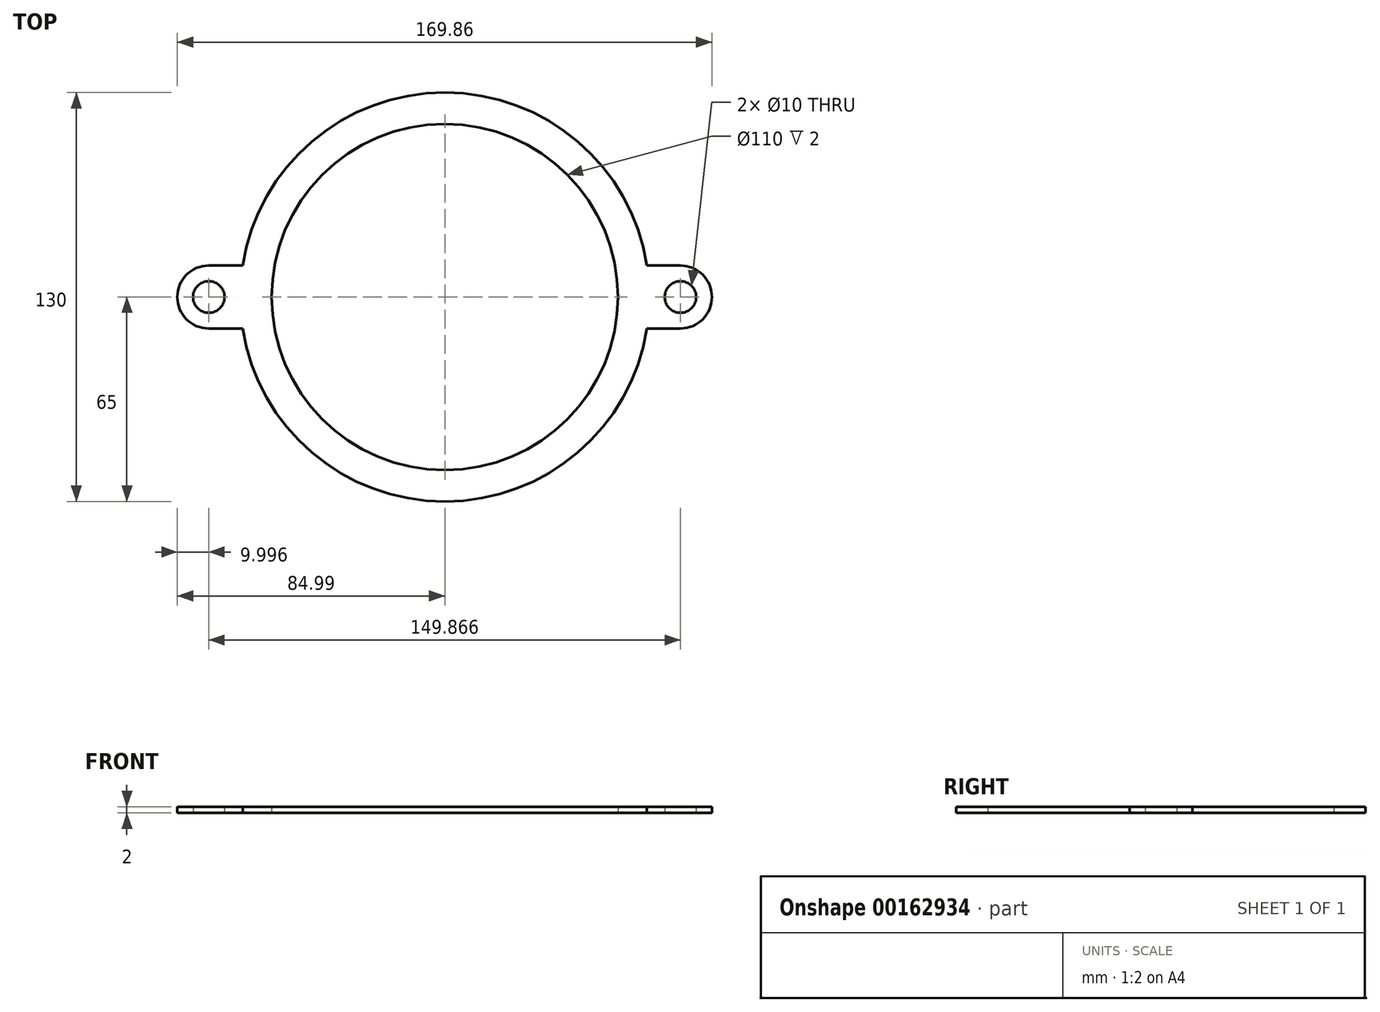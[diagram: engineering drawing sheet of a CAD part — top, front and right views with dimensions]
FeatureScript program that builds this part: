
annotation { "Feature Type Name" : "Feature", "Feature Type Description" : "" }
export const myFeature = defineFeature(function(context is Context, id is Id, definition is map)
    precondition{}
    {
        {
            var Q0;
            Q0=qCreatedBy(makeId("Top.planeOp"),FACE);
            var sketch = newSketch(context, id + "F0", { "sketchPlane" : qUnion([Q0])});
            skCircle(sketch, "E0", {"center": v(0, 0) * mm, "radius": 65 * mm});
            skCircle(sketch, "E1", {"center": v(0, 0) * mm, "radius": 55 * mm});
            skLineSegment(sketch, "E2.bottom", {"start": v(85, 10) * mm, "end": v(-85, 10) * mm});
            skLineSegment(sketch, "E2.top", {"start": v(85, -10) * mm, "end": v(-85, -10) * mm});
            skLineSegment(sketch, "E2.left", {"start": v(85, 10) * mm, "end": v(85, -10) * mm});
            skLineSegment(sketch, "E2.right", {"start": v(-85, 10) * mm, "end": v(-85, -10) * mm});
            skCircle(sketch, "E3", {"center": v(-75, 0) * mm, "radius": 10 * mm});
            skCircle(sketch, "E4", {"center": v(-75, 0) * mm, "radius": 5 * mm});
            skCircle(sketch, "E5", {"center": v(74.87, 0) * mm, "radius": 10 * mm});
            skCircle(sketch, "E6", {"center": v(74.87, 0) * mm, "radius": 5 * mm});
            skSolve(sketch);
        }
        {
            var Q0;
            {var subQ0=sQuery(id+"F0.wireOp",EDGE,"E2.bottom");var subQ1=sQuery(id+"F0.wireOp",EDGE,"E0");var subQ2=makeQuery(id+"F0.imprint","INTERSECT",VERTEX,{"disambiguationData":[OD(0.0)],"derivedFrom":[subQ1,subQ0]});Q0=makeQuery(id+"F0.imprint","IMPRINT",FACE,{"disambiguationData":[TD([[makeQuery(id+"F0.imprint","IMPRINT",EDGE,{"disambiguationData":[TD([[subQ2,-1.0]])],"derivedFrom":subQ1}),1.0]])]});}
            var Q1;
            {var subQ0=sQuery(id+"F0.wireOp",EDGE,"E2.bottom");var subQ1=sQuery(id+"F0.wireOp",EDGE,"E0");var subQ2=makeQuery(id+"F0.imprint","INTERSECT",VERTEX,{"disambiguationData":[OD(0.0)],"derivedFrom":[subQ1,subQ0]});Q1=makeQuery(id+"F0.imprint","IMPRINT",FACE,{"disambiguationData":[TD([[makeQuery(id+"F0.imprint","IMPRINT",EDGE,{"disambiguationData":[TD([[subQ2,1.0]])],"derivedFrom":subQ1}),1.0]])]});}
            var Q2;
            {var subQ0=sQuery(id+"F0.wireOp",EDGE,"E2.bottom");var subQ1=sQuery(id+"F0.wireOp",EDGE,"E0");var subQ2=makeQuery(id+"F0.imprint","INTERSECT",VERTEX,{"disambiguationData":[OD(0.0)],"derivedFrom":[subQ1,subQ0]});Q2=makeQuery(id+"F0.imprint","IMPRINT",FACE,{"disambiguationData":[TD([[makeQuery(id+"F0.imprint","IMPRINT",EDGE,{"disambiguationData":[TD([[subQ2,1.0]])],"derivedFrom":subQ1}),-1.0]])]});}
            var Q3;
            Q3=makeQuery(id+"F0.imprint","IMPRINT",FACE,{"disambiguationData":[TD([[makeQuery(id+"F0.imprint","IMPRINT",EDGE,{"derivedFrom":sQuery(id+"F0.wireOp",EDGE,"E6")}),-1.0]])]});
            var Q4;
            {var subQ0=sQuery(id+"F0.wireOp",EDGE,"E2.top");var subQ1=sQuery(id+"F0.wireOp",EDGE,"E0");var subQ2=makeQuery(id+"F0.imprint","INTERSECT",VERTEX,{"disambiguationData":[OD(1.0)],"derivedFrom":[subQ1,subQ0]});Q4=makeQuery(id+"F0.imprint","IMPRINT",FACE,{"disambiguationData":[TD([[makeQuery(id+"F0.imprint","IMPRINT",EDGE,{"disambiguationData":[TD([[subQ2,-1.0]])],"derivedFrom":subQ1}),-1.0]])]});}
            var Q5;
            {var subQ0=sQuery(id+"F0.wireOp",EDGE,"E2.top");var subQ1=sQuery(id+"F0.wireOp",EDGE,"E0");var subQ2=makeQuery(id+"F0.imprint","INTERSECT",VERTEX,{"disambiguationData":[OD(0.0)],"derivedFrom":[subQ1,subQ0]});Q5=makeQuery(id+"F0.imprint","IMPRINT",FACE,{"disambiguationData":[TD([[makeQuery(id+"F0.imprint","IMPRINT",EDGE,{"disambiguationData":[TD([[subQ2,-1.0]])],"derivedFrom":subQ1}),1.0]])]});}
            var Q6;
            Q6=makeQuery(id+"F0.imprint","IMPRINT",FACE,{"disambiguationData":[TD([[makeQuery(id+"F0.imprint","IMPRINT",EDGE,{"derivedFrom":sQuery(id+"F0.wireOp",EDGE,"E4")}),-1.0]])]});
            var Q7;
            {var subQ0=sQuery(id+"F0.wireOp",EDGE,"E2.top");var subQ1=sQuery(id+"F0.wireOp",EDGE,"E0");var subQ2=makeQuery(id+"F0.imprint","INTERSECT",VERTEX,{"disambiguationData":[OD(0.0)],"derivedFrom":[subQ1,subQ0]});Q7=makeQuery(id+"F0.imprint","IMPRINT",FACE,{"disambiguationData":[TD([[makeQuery(id+"F0.imprint","IMPRINT",EDGE,{"disambiguationData":[TD([[subQ2,1.0]])],"derivedFrom":subQ1}),-1.0]])]});}
            var Q8;
            {var subQ0=sQuery(id+"F0.wireOp",EDGE,"E2.bottom");var subQ1=sQuery(id+"F0.wireOp",EDGE,"E0");var subQ2=makeQuery(id+"F0.imprint","INTERSECT",VERTEX,{"disambiguationData":[OD(1.0)],"derivedFrom":[subQ1,subQ0]});Q8=makeQuery(id+"F0.imprint","IMPRINT",FACE,{"disambiguationData":[TD([[makeQuery(id+"F0.imprint","IMPRINT",EDGE,{"disambiguationData":[TD([[subQ2,-1.0]])],"derivedFrom":subQ1}),-1.0]])]});}
            var Q9;
            {var subQ0=sQuery(id+"F0.wireOp",EDGE,"E2.bottom");var subQ5=sQuery(id+"F0.wireOp",EDGE,"E0");var subQ6=makeQuery(id+"F0.imprint","INTERSECT",VERTEX,{"disambiguationData":[OD(1.0)],"derivedFrom":[subQ5,subQ0]});Q9=makeQuery(id+"F0.imprint","IMPRINT",FACE,{"disambiguationData":[TD([[makeQuery(id+"F0.imprint","IMPRINT",EDGE,{"disambiguationData":[TD([[subQ6,-1.0]])],"derivedFrom":subQ5}),1.0]])]});}
            var Q10;
            {var subQ0=sQuery(id+"F0.wireOp",EDGE,"E3");var subQ1=sQuery(id+"F0.wireOp",EDGE,"E0");var subQ2=makeQuery(id+"F0.imprint","INTERSECT",VERTEX,{"disambiguationData":[OD(0.0)],"derivedFrom":[subQ1,subQ0]});Q10=makeQuery(id+"F0.imprint","IMPRINT",FACE,{"disambiguationData":[TD([[makeQuery(id+"F0.imprint","IMPRINT",EDGE,{"disambiguationData":[TD([[subQ2,-1.0]])],"derivedFrom":subQ1}),1.0]])]});}
            var Q11;
            {var subQ0=sQuery(id+"F0.wireOp",EDGE,"E5");var subQ1=sQuery(id+"F0.wireOp",EDGE,"E0");var subQ2=makeQuery(id+"F0.imprint","INTERSECT",VERTEX,{"disambiguationData":[OD(0.0)],"derivedFrom":[subQ1,subQ0]});Q11=makeQuery(id+"F0.imprint","IMPRINT",FACE,{"disambiguationData":[TD([[makeQuery(id+"F0.imprint","IMPRINT",EDGE,{"disambiguationData":[TD([[subQ2,1.0]])],"derivedFrom":subQ1}),1.0]])]});}
            extrude(context, id + "F1", {"entities" : qUnion([Q0, Q1, Q2, Q3, Q4, Q5, Q6, Q7, Q8, Q9, Q10, Q11]), "depth" : 2 * mm});
        }
    });
